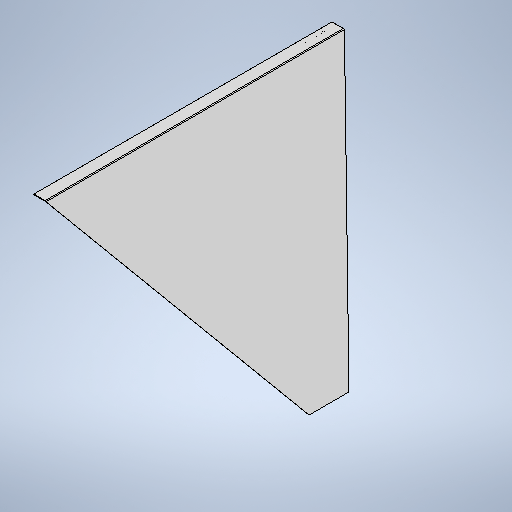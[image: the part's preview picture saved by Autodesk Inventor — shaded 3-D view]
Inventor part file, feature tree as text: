
AUTODESK INVENTOR PART (.ipt)
format: ipt  version: 2025 (Build 290162010, 162A)  size: 348,672 bytes
history: native  units: mm
features: other x5, sheet_metal_op x3, sketch x3, reference x2, extrude x1
ambient origin geometry x8: Origin, YZ Plane, XZ Plane, XY Plane, X Axis, Y Axis, Z Axis, Center Point
bodies: Solid1 (feature_tree)
feature tree (14):
  sheet_metal_op  "Contour Flange1"
  extrude  "Extrusion9"  Depth=4.0mm
  other  "Mark2"
  sketch  "Sketch1"  dims[d6=4.0mm d7=4.0mm]
  other  "Plate1"
  sheet_metal_op  "Bend1"
  sheet_metal_op  "Corner1"
  sketch  "Sketch12"  dims[d8=2.0mm]
  reference  "Reference1"
  reference  "Reference2"
  sketch  "Sketch14"  dims[d9=8.0mm d10=6.0mm d11=1500.0mm d12=6.0mm d13=4.0mm d14=16.0mm d15=4.0mm d16=6.0mm d61=100.0mm d65=230.0mm d66=1150.0mm d68=60.0mm d70=6.0mm d79=775.0mm d81=6.0mm d82=0.0mm d83=0.0mm]
  other  "ASY MSC 100 cone.iam"
  other  "MSC 114 cone IN right board.ipt:1"
  other  "MSC 113 cone IN left board.ipt:1"
